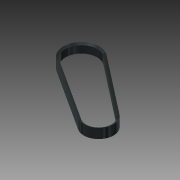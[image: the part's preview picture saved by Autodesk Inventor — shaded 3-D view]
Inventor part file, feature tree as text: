
AUTODESK INVENTOR PART (.ipt)
format: ipt  version: 2015 (Build 190159000, 159)  size: 103,424 bytes
history: native  units: mm
features: chamfer x2, extrude x1, sketch x1
ambient origin geometry x8: Origin, YZ Plane, XZ Plane, XY Plane, X Axis, Y Axis, Z Axis, Center Point
bodies: 实体1 (feature_tree)
feature tree (4):
  extrude  "拉伸1"  Depth=3.5mm
  chamfer  "倒角1"  Distance=95.0mm
  chamfer  "倒角2"  Distance=67.5mm
  sketch  "草图1"  dims[d0=50.0mm d1=40.0mm d2=95.0mm d3=67.5mm d4=3.5mm d5=3.5mm d6=15.423mm d7=0.0mm d8=3.5mm d9=2.021mm d10=60.0deg d11=3.5mm d12=2.021mm d13=60.0deg]
